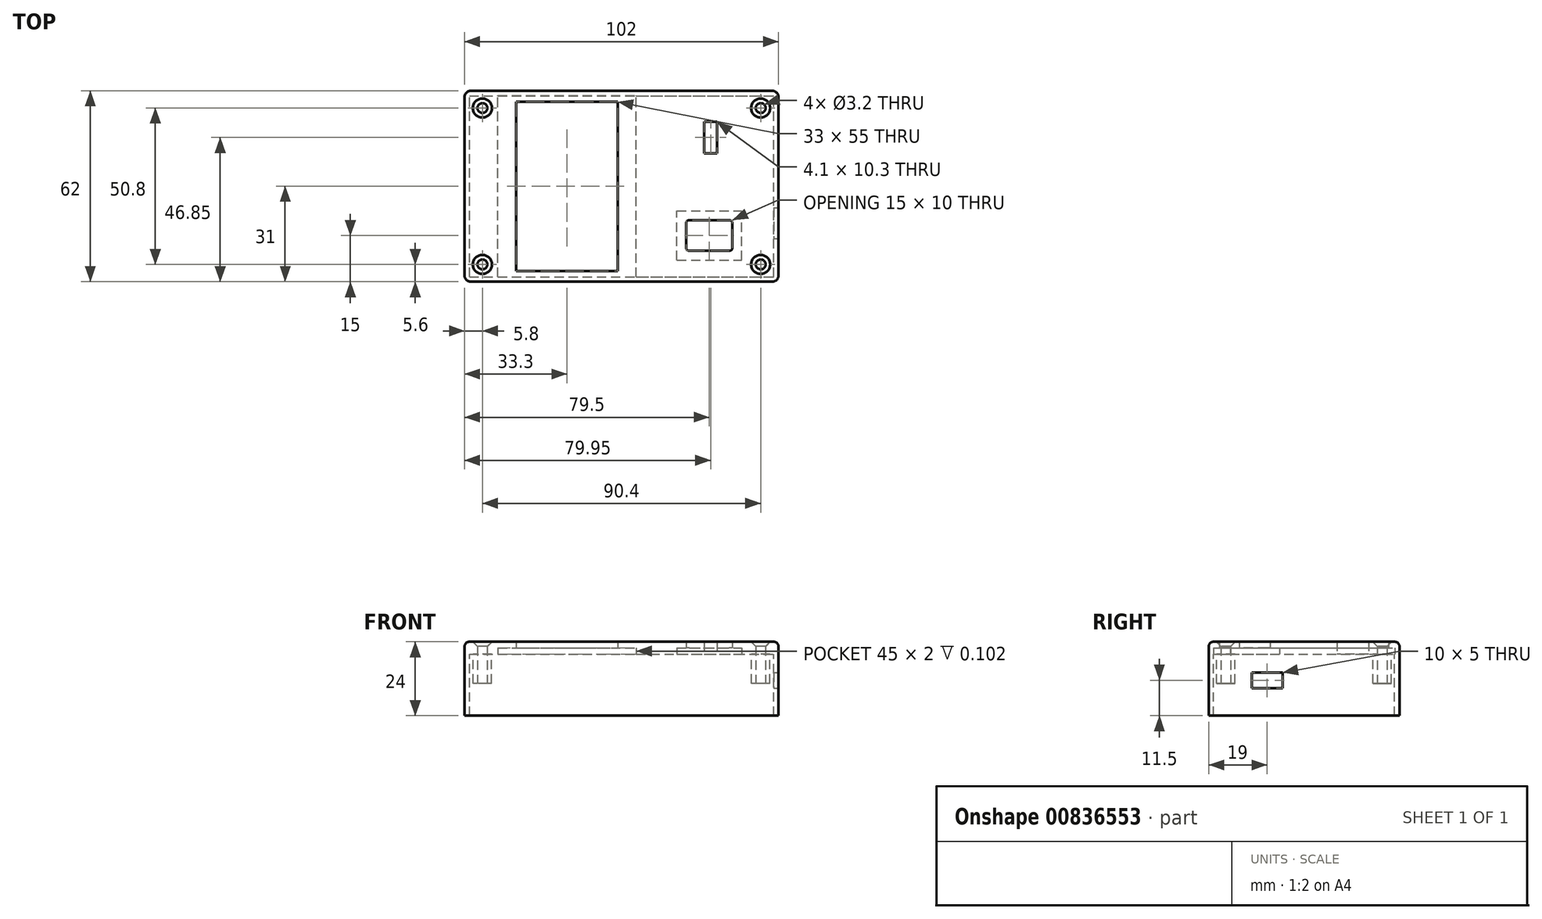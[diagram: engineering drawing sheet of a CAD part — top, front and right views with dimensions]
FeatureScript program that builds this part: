
annotation { "Feature Type Name" : "Feature", "Feature Type Description" : "" }
export const myFeature = defineFeature(function(context is Context, id is Id, definition is map)
    precondition{}
    {
        {
            var Q0;
            Q0=qCreatedBy(makeId("Top.planeOp"),FACE);
            var sketch = newSketch(context, id + "F0", { "sketchPlane" : qUnion([Q0]), "disableImprinting" : false});
            skLineSegment(sketch, "E0.bottom", {"start": v(0, 0) * mm, "end": v(-102, 0) * mm});
            skLineSegment(sketch, "E0.top", {"start": v(0, 62) * mm, "end": v(-102, 62) * mm});
            skLineSegment(sketch, "E0.left", {"start": v(0, 0) * mm, "end": v(0, 62) * mm});
            skLineSegment(sketch, "E0.right", {"start": v(-102, 0) * mm, "end": v(-102, 62) * mm});
            skLineSegment(sketch, "E1.bottom", {"start": v(-85.2, 3.5) * mm, "end": v(-52.2, 3.5) * mm});
            skLineSegment(sketch, "E1.top", {"start": v(-85.2, 58.5) * mm, "end": v(-52.2, 58.5) * mm});
            skLineSegment(sketch, "E1.left", {"start": v(-85.2, 3.5) * mm, "end": v(-85.2, 58.5) * mm});
            skLineSegment(sketch, "E1.right", {"start": v(-52.2, 3.5) * mm, "end": v(-52.2, 58.5) * mm});
            skCircle(sketch, "E2", {"center": v(-5.8, 5.6) * mm, "radius": 1.6 * mm});
            skCircle(sketch, "E3", {"center": v(-5.8, 56.4) * mm, "radius": 1.6 * mm});
            skCircle(sketch, "E4", {"center": v(-96.2, 5.6) * mm, "radius": 1.6 * mm});
            skCircle(sketch, "E5", {"center": v(-96.2, 56.4) * mm, "radius": 1.6 * mm});
            skLineSegment(sketch, "E6.bottom", {"start": v(-29, 20) * mm, "end": v(-16, 20) * mm});
            skLineSegment(sketch, "E6.top", {"start": v(-29, 10) * mm, "end": v(-16, 10) * mm});
            skLineSegment(sketch, "E6.left", {"start": v(-30, 19) * mm, "end": v(-30, 11) * mm});
            skLineSegment(sketch, "E6.right", {"start": v(-15, 19) * mm, "end": v(-15, 11) * mm});
            skPoint(sketch, "E7.visualSharp", {"position": v(-30, 20) * mm});
            skArc(sketch, "E7.filletArc", {"start": v(-29, 20) * mm, "mid": v(-29.7, 19.7) * mm, "end": v(-30, 19) * mm});
            skPoint(sketch, "E8.visualSharp", {"position": v(-15, 20) * mm});
            skArc(sketch, "E8.filletArc", {"start": v(-15, 19) * mm, "mid": v(-15.3, 19.7) * mm, "end": v(-16, 20) * mm});
            skPoint(sketch, "E9.visualSharp", {"position": v(-30, 10) * mm});
            skArc(sketch, "E9.filletArc", {"start": v(-30, 11) * mm, "mid": v(-29.7, 10.3) * mm, "end": v(-29, 10) * mm});
            skPoint(sketch, "E10.visualSharp", {"position": v(-15, 10) * mm});
            skArc(sketch, "E10.filletArc", {"start": v(-16, 10) * mm, "mid": v(-15.3, 10.3) * mm, "end": v(-15, 11) * mm});
            skLineSegment(sketch, "E11.bottom", {"start": v(-24.1, 52) * mm, "end": v(-20, 52) * mm});
            skLineSegment(sketch, "E11.top", {"start": v(-24.1, 41.7) * mm, "end": v(-20, 41.7) * mm});
            skLineSegment(sketch, "E11.left", {"start": v(-24.1, 52) * mm, "end": v(-24.1, 41.7) * mm});
            skLineSegment(sketch, "E11.right", {"start": v(-20, 52) * mm, "end": v(-20, 41.7) * mm});
            skSolve(sketch);
        }
        {
            var Q0;
            Q0=makeQuery(id+"F0.imprint","IMPRINT",FACE,{"disambiguationData":[TD([[makeQuery(id+"F0.imprint","IMPRINT",EDGE,{"derivedFrom":sQuery(id+"F0.wireOp",EDGE,"E0.bottom")}),-1.0]])]});
            extrude(context, id + "F1", {"entities" : qUnion([Q0]), "depth" : 4 * mm, "offsetDistance" : 25 * mm});
        }
        {
            var Q0;
            Q0=makeQuery(id+"F1.opExtrude","CAP_EDGE",EDGE,{"disambiguationData":[OSD([sQuery(id+"F0.wireOp",EDGE,"E0.top")])],"isStart":false});
            var Q1;
            Q1=makeQuery(id+"F1.opExtrude","CAP_EDGE",EDGE,{"disambiguationData":[OSD([sQuery(id+"F0.wireOp",EDGE,"E0.right")])],"isStart":false});
            var Q2;
            Q2=makeQuery(id+"F1.opExtrude","CAP_EDGE",EDGE,{"disambiguationData":[OSD([sQuery(id+"F0.wireOp",EDGE,"E0.bottom")])],"isStart":false});
            var Q3;
            Q3=makeQuery(id+"F1.opExtrude","CAP_EDGE",EDGE,{"disambiguationData":[OSD([sQuery(id+"F0.wireOp",EDGE,"E0.left")])],"isStart":false});
            fillet(context, id + "F2", {"entities" : qUnion([Q0, Q1, Q2, Q3]), "radius" : 1.5 * mm, "tangentPropagation" : true, "allowEdgeOverflow" : false});
        }
        {
            var Q0;
            Q0=makeQuery(id+"F1.opExtrude","CAP_FACE",FACE,{"disambiguationData":[OSD([sQuery(id+"F0.wireOp",EDGE,"E0.bottom"),sQuery(id+"F0.wireOp",EDGE,"E0.top"),sQuery(id+"F0.wireOp",EDGE,"E0.left"),sQuery(id+"F0.wireOp",EDGE,"E0.right"),sQuery(id+"F0.wireOp",EDGE,"E1.bottom"),sQuery(id+"F0.wireOp",EDGE,"E1.top"),sQuery(id+"F0.wireOp",EDGE,"E1.left"),sQuery(id+"F0.wireOp",EDGE,"E1.right"),sQuery(id+"F0.wireOp",EDGE,"E2"),sQuery(id+"F0.wireOp",EDGE,"E3"),sQuery(id+"F0.wireOp",EDGE,"E4"),sQuery(id+"F0.wireOp",EDGE,"E5")])],"isStart":true});
            var sketch = newSketch(context, id + "F3", { "sketchPlane" : qUnion([Q0])});
            skLineSegment(sketch, "E12.bottom", {"start": v(-102, 0) * mm, "end": v(0, 0) * mm});
            skLineSegment(sketch, "E12.top", {"start": v(-102, -62) * mm, "end": v(0, -62) * mm});
            skLineSegment(sketch, "E12.left", {"start": v(-102, 0) * mm, "end": v(-102, -62) * mm});
            skLineSegment(sketch, "E12.right", {"start": v(0, 0) * mm, "end": v(0, -62) * mm});
            skLineSegment(sketch, "E13.bottom", {"start": v(-100.4, -1.6) * mm, "end": v(-1.6, -1.6) * mm});
            skLineSegment(sketch, "E13.top", {"start": v(-100.4, -60.4) * mm, "end": v(-1.6, -60.4) * mm});
            skLineSegment(sketch, "E13.left", {"start": v(-100.4, -1.6) * mm, "end": v(-100.4, -60.4) * mm});
            skLineSegment(sketch, "E13.right", {"start": v(-1.6, -1.6) * mm, "end": v(-1.6, -60.4) * mm});
            skSolve(sketch);
        }
        {
            var Q0;
            Q0=makeQuery(id+"F3.imprint","IMPRINT",FACE,{"disambiguationData":[TD([[makeQuery(id+"F3.imprint","IMPRINT",EDGE,{"derivedFrom":sQuery(id+"F3.wireOp",EDGE,"E12.bottom")}),1.0]])]});
            var Q1;
            Q1 = qSketchRegion(id + "F5", true);
            extrude(context, id + "F4", {"entities" : qUnion([Q0, Q1]), "operationType" : NewBodyOperationType.ADD, "depth" : 20 * mm, "offsetDistance" : 25 * mm});
        }
        {
            var Q0;
            Q0=makeQuery(id+"FT1tWLzNTIapuoo_1.boolean.opBoolean","MERGE",FACE,{"derivedFrom":[makeQuery(id+"F4.boolean.opBoolean","MERGE",FACE,{"derivedFrom":[makeQuery(id+"F1.opExtrude","SWEPT_FACE",FACE,{"disambiguationData":[OSD([sQuery(id+"F0.wireOp",EDGE,"E0.left")])]}),makeQuery(id+"F4.opExtrude","SWEPT_FACE",FACE,{"disambiguationData":[OSD([sQuery(id+"F3.wireOp",EDGE,"E12.right")])]})]}),makeQuery(id+"FT1tWLzNTIapuoo_1.opExtrude","SWEPT_FACE",FACE,{"disambiguationData":[OSD([sQuery(id+"F3i6GuYPQumQxPC_1.wireOp",EDGE,"OneAktyi-rDek-kPKx-T9Jq-bFhZZVmPXhrr.right")])]})]});
            var sketch = newSketch(context, id + "F5", { "sketchPlane" : qUnion([Q0])});
            skLineSegment(sketch, "E14.bottom", {"start": v(24, -6) * mm, "end": v(14, -6) * mm});
            skLineSegment(sketch, "E14.top", {"start": v(24, -11) * mm, "end": v(14, -11) * mm});
            skLineSegment(sketch, "E14.left", {"start": v(24, -6) * mm, "end": v(24, -11) * mm});
            skLineSegment(sketch, "E14.right", {"start": v(14, -6) * mm, "end": v(14, -11) * mm});
            skSolve(sketch);
        }
        {
            var Q0;
            Q0=makeQuery(id+"F5.imprint","IMPRINT",FACE,{"disambiguationData":[TD([[makeQuery(id+"F5.imprint","IMPRINT",EDGE,{"derivedFrom":sQuery(id+"F5.wireOp",EDGE,"E14.bottom")}),1.0]])]});
            extrude(context, id + "F6", {"entities" : qUnion([Q0]), "operationType" : NewBodyOperationType.REMOVE, "oppositeDirection" : true, "depth" : 25 * mm, "offsetDistance" : 25 * mm});
        }
        {
            var Q0;
            Q0=makeQuery(id+"F4.boolean.opBoolean","MERGE",EDGE,{"derivedFrom":[makeQuery(id+"F1.opExtrude","SWEPT_EDGE",EDGE,{"disambiguationData":[OSD([sQuery(id+"F0.wireOp",EDGE,"E0.bottom"),sQuery(id+"F0.wireOp",EDGE,"E0.left")])]}),makeQuery(id+"F4.opExtrude","SWEPT_EDGE",EDGE,{"disambiguationData":[OSD([sQuery(id+"F3.wireOp",EDGE,"E12.bottom"),sQuery(id+"F3.wireOp",EDGE,"E12.right")])]})]});
            var Q1;
            Q1=makeQuery(id+"F4.boolean.opBoolean","MERGE",EDGE,{"derivedFrom":[makeQuery(id+"F1.opExtrude","SWEPT_EDGE",EDGE,{"disambiguationData":[OSD([sQuery(id+"F0.wireOp",EDGE,"E0.bottom"),sQuery(id+"F0.wireOp",EDGE,"E0.right")])]}),makeQuery(id+"F4.opExtrude","SWEPT_EDGE",EDGE,{"disambiguationData":[OSD([sQuery(id+"F3.wireOp",EDGE,"E12.bottom"),sQuery(id+"F3.wireOp",EDGE,"E12.left")])]})]});
            var Q2;
            Q2=makeQuery(id+"F4.boolean.opBoolean","MERGE",EDGE,{"derivedFrom":[makeQuery(id+"F1.opExtrude","SWEPT_EDGE",EDGE,{"disambiguationData":[OSD([sQuery(id+"F0.wireOp",EDGE,"E0.top"),sQuery(id+"F0.wireOp",EDGE,"E0.left")])]}),makeQuery(id+"F4.opExtrude","SWEPT_EDGE",EDGE,{"disambiguationData":[OSD([sQuery(id+"F3.wireOp",EDGE,"E12.top"),sQuery(id+"F3.wireOp",EDGE,"E12.right")])]})]});
            var Q3;
            Q3=makeQuery(id+"F4.boolean.opBoolean","MERGE",EDGE,{"derivedFrom":[makeQuery(id+"F1.opExtrude","SWEPT_EDGE",EDGE,{"disambiguationData":[OSD([sQuery(id+"F0.wireOp",EDGE,"E0.top"),sQuery(id+"F0.wireOp",EDGE,"E0.right")])]}),makeQuery(id+"F4.opExtrude","SWEPT_EDGE",EDGE,{"disambiguationData":[OSD([sQuery(id+"F3.wireOp",EDGE,"E12.top"),sQuery(id+"F3.wireOp",EDGE,"E12.left")])]})]});
            fillet(context, id + "F7", {"entities" : qUnion([Q0, Q1, Q2, Q3]), "radius" : 2 * mm, "tangentPropagation" : true, "allowEdgeOverflow" : false});
        }
        {
            var Q0;
            Q0=makeQuery(id+"F0.imprint","IMPRINT",FACE,{"disambiguationData":[TD([[makeQuery(id+"F0.imprint","IMPRINT",EDGE,{"derivedFrom":sQuery(id+"F0.wireOp",EDGE,"E4")}),1.0]])]});
            var sketch = newSketch(context, id + "F8", { "sketchPlane" : qUnion([Q0])});
            skCircle(sketch, "E15", {"center": v(-96.2, 5.6) * mm, "radius": 3 * mm});
            skCircle(sketch, "E16", {"center": v(-96.2, 56.4) * mm, "radius": 3 * mm});
            skCircle(sketch, "E17", {"center": v(-5.8, 56.4) * mm, "radius": 3 * mm});
            skCircle(sketch, "E18", {"center": v(-5.8, 5.6) * mm, "radius": 3 * mm});
            skSolve(sketch);
        }
        {
            var Q0;
            Q0 = qSketchRegion(id + "F8", true);
            extrude(context, id + "F9", {"entities" : qUnion([Q0]), "operationType" : NewBodyOperationType.ADD, "oppositeDirection" : true, "depth" : 9.5 * mm, "offsetDistance" : 25 * mm});
        }
        {
            var Q0;
            Q0=makeQuery(id+"F0.imprint","IMPRINT",FACE,{"disambiguationData":[TD([[makeQuery(id+"F0.imprint","IMPRINT",EDGE,{"derivedFrom":sQuery(id+"F0.wireOp",EDGE,"E4")}),1.0]])]});
            var Q1;
            Q1=makeQuery(id+"F0.imprint","IMPRINT",FACE,{"disambiguationData":[TD([[makeQuery(id+"F0.imprint","IMPRINT",EDGE,{"derivedFrom":sQuery(id+"F0.wireOp",EDGE,"E5")}),1.0]])]});
            var Q2;
            Q2=makeQuery(id+"F0.imprint","IMPRINT",FACE,{"disambiguationData":[TD([[makeQuery(id+"F0.imprint","IMPRINT",EDGE,{"derivedFrom":sQuery(id+"F0.wireOp",EDGE,"E3")}),1.0]])]});
            var Q3;
            Q3=makeQuery(id+"F0.imprint","IMPRINT",FACE,{"disambiguationData":[TD([[makeQuery(id+"F0.imprint","IMPRINT",EDGE,{"derivedFrom":sQuery(id+"F0.wireOp",EDGE,"E2")}),1.0]])]});
            extrude(context, id + "F10", {"entities" : qUnion([Q0, Q1, Q2, Q3]), "operationType" : NewBodyOperationType.REMOVE, "oppositeDirection" : true, "depth" : 9.5 * mm, "offsetDistance" : 25 * mm});
        }
        {
            var Q0;
            Q0=makeQuery(id+"F0.imprint","IMPRINT",FACE,{"disambiguationData":[TD([[makeQuery(id+"F0.imprint","IMPRINT",EDGE,{"derivedFrom":sQuery(id+"F0.wireOp",EDGE,"E0.bottom")}),-1.0]])]});
            var sketch = newSketch(context, id + "F11", { "sketchPlane" : qUnion([Q0])});
            skLineSegment(sketch, "E19.bottom", {"start": v(-91.2, 1.5) * mm, "end": v(-46.2, 1.5) * mm});
            skLineSegment(sketch, "E19.top", {"start": v(-91.2, 60.5) * mm, "end": v(-46.2, 60.5) * mm});
            skLineSegment(sketch, "E19.left", {"start": v(-91.2, 1.5) * mm, "end": v(-91.2, 60.5) * mm});
            skLineSegment(sketch, "E19.right", {"start": v(-46.2, 1.5) * mm, "end": v(-46.2, 60.5) * mm});
            skLineSegment(sketch, "E20.bottom", {"start": v(-33, 7) * mm, "end": v(-12, 7) * mm});
            skLineSegment(sketch, "E20.top", {"start": v(-33, 23) * mm, "end": v(-12, 23) * mm});
            skLineSegment(sketch, "E20.left", {"start": v(-33, 7) * mm, "end": v(-33, 23) * mm});
            skLineSegment(sketch, "E20.right", {"start": v(-12, 7) * mm, "end": v(-12, 23) * mm});
            skSolve(sketch);
        }
        {
            var Q0;
            Q0 = qSketchRegion(id + "F11", true);
            extrude(context, id + "F12", {"entities" : qUnion([Q0]), "operationType" : NewBodyOperationType.REMOVE, "oppositeDirection" : true, "depth" : -2 * mm, "offsetDistance" : 25 * mm});
        }
        {
            var Q0;
            Q0=makeQuery(id+"F1.opExtrude","CAP_EDGE",EDGE,{"disambiguationData":[OSD([sQuery(id+"F0.wireOp",EDGE,"E2")])],"isStart":false});
            var Q1;
            Q1=makeQuery(id+"F1.opExtrude","CAP_EDGE",EDGE,{"disambiguationData":[OSD([sQuery(id+"F0.wireOp",EDGE,"E3")])],"isStart":false});
            var Q2;
            Q2=makeQuery(id+"F1.opExtrude","CAP_EDGE",EDGE,{"disambiguationData":[OSD([sQuery(id+"F0.wireOp",EDGE,"E4")])],"isStart":false});
            var Q3;
            Q3=makeQuery(id+"F1.opExtrude","CAP_EDGE",EDGE,{"disambiguationData":[OSD([sQuery(id+"F0.wireOp",EDGE,"E5")])],"isStart":false});
            chamfer(context, id + "F13", {"entities" : qUnion([Q0, Q1, Q2, Q3]), "chamferType" : ChamferType.OFFSET_ANGLE, "width" : 1.5 * mm, "oppositeDirection" : false, "angle" : 45 * degree, "tangentPropagation" : true});
        }
    });
